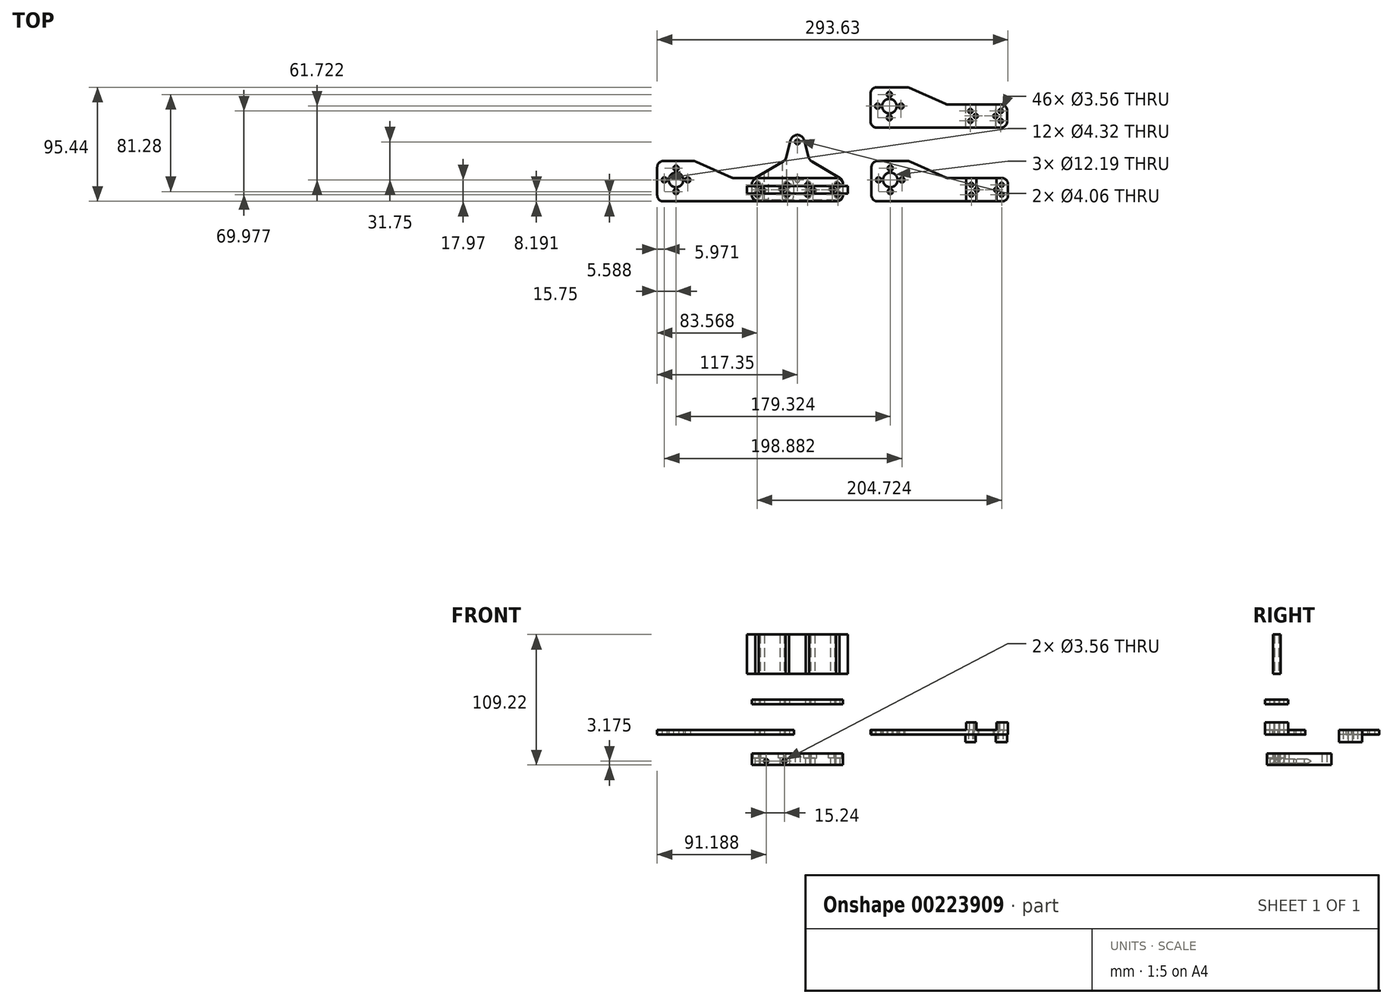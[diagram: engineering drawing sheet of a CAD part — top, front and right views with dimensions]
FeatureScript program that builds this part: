
annotation { "Feature Type Name" : "Feature", "Feature Type Description" : "" }
export const myFeature = defineFeature(function(context is Context, id is Id, definition is map)
    precondition{}
    {
        {
            var Q0;
            Q0=qCreatedBy(makeId("Top.planeOp"),FACE);
            var sketch = newSketch(context, id + "F0", { "sketchPlane" : qUnion([Q0])});
            skCircle(sketch, "E0", {"center": v(0, 37.5) * mm, "radius": 2.03 * mm});
            skCircle(sketch, "E1", {"center": v(0, 5.75) * mm, "radius": 2.03 * mm});
            skCircle(sketch, "E2", {"center": v(0, 37.5) * mm, "radius": 5.84 * mm});
            skLineSegment(sketch, "E3", {"start": v(-10.16, 22.26) * mm, "end": v(-5.64, 39.02) * mm});
            skLineSegment(sketch, "E4", {"start": v(10.16, 22.26) * mm, "end": v(5.64, 39.02) * mm});
            skPoint(sketch, "E5.orphan", {"position": v(0, 22.26) * mm});
            skLineSegment(sketch, "E6", {"start": v(-38.1, -10.76) * mm, "end": v(38.1, -10.76) * mm});
            skLineSegment(sketch, "E7", {"start": v(-38.1, -10.76) * mm, "end": v(-38.1, 5.75) * mm});
            skLineSegment(sketch, "E8", {"start": v(38.1, 5.75) * mm, "end": v(38.1, -10.76) * mm});
            skLineSegment(sketch, "E9", {"start": v(-10.16, 22.26) * mm, "end": v(10.16, 22.26) * mm});
            skLineSegment(sketch, "E10", {"start": v(-38.1, 5.75) * mm, "end": v(-10.16, 22.26) * mm});
            skLineSegment(sketch, "E11", {"start": v(10.16, 22.26) * mm, "end": v(38.1, 5.75) * mm});
            skPoint(sketch, "E12.centerSnap0", {"position": v(38.1, -2.5) * mm});
            skPoint(sketch, "E13.centerSnap0", {"position": v(-38.1, -2.5) * mm});
            skCircle(sketch, "E14.MirrorC", {"center": v(33.78, -6.63) * mm, "radius": 1.78 * mm});
            skCircle(sketch, "E15.MirrorC", {"center": v(33.78, 1.62) * mm, "radius": 1.78 * mm});
            skCircle(sketch, "E16", {"center": v(8.38, 1.62) * mm, "radius": 1.78 * mm});
            skCircle(sketch, "E17", {"center": v(8.38, -6.63) * mm, "radius": 1.78 * mm});
            skCircle(sketch, "E18.MirrorC", {"center": v(-8.38, -6.63) * mm, "radius": 1.78 * mm});
            skCircle(sketch, "E19.MirrorC", {"center": v(-33.78, -6.63) * mm, "radius": 1.78 * mm});
            skCircle(sketch, "E20.MirrorC", {"center": v(-33.78, 1.62) * mm, "radius": 1.78 * mm});
            skCircle(sketch, "E21.MirrorC", {"center": v(-8.38, 1.62) * mm, "radius": 1.78 * mm});
            skCircle(sketch, "E22", {"center": v(-29.3, -2.5) * mm, "radius": 1.78 * mm});
            skCircle(sketch, "E23", {"center": v(-12.87, -2.5) * mm, "radius": 1.78 * mm});
            skCircle(sketch, "E24.MirrorC", {"center": v(12.87, -2.5) * mm, "radius": 1.78 * mm});
            skCircle(sketch, "E25.MirrorC", {"center": v(29.3, -2.5) * mm, "radius": 1.78 * mm});
            skSolve(sketch);
        }
        {
            var Q0;
            Q0=qSketchRegion(id+"F0",true);
            extrude(context, id + "F1", {"entities" : qUnion([Q0]), "depth" : 9.65 * mm});
        }
        {
            var Q0;
            Q0=makeQuery(id+"FxuT3BSMLhrPvgB_1.opExtrude","SWEPT_EDGE",EDGE,{"disambiguationData":[OSD([sQuery(id+"FRq1eFHlobFPW3q_1.wireOp",EDGE,"58NqGU18-HprJ-QbKg-xDFZ-83wXZvhciFSB"),sQuery(id+"FRq1eFHlobFPW3q_1.wireOp",EDGE,"uo3OqS3Z-w3Q3-Ubee-oUpL-cwzrscQqbqLB")])]});
            var Q1;
            Q1=makeQuery(id+"FxuT3BSMLhrPvgB_1.opExtrude","SWEPT_EDGE",EDGE,{"disambiguationData":[OSD([sQuery(id+"FRq1eFHlobFPW3q_1.wireOp",EDGE,"0EPiVd3f-FInE-hob0-EaqF-tfDaMfGh4eWV.bottom"),sQuery(id+"FRq1eFHlobFPW3q_1.wireOp",EDGE,"uo3OqS3Z-w3Q3-Ubee-oUpL-cwzrscQqbqLB")])]});
            var Q2;
            Q2=makeQuery(id+"FxuT3BSMLhrPvgB_1.opExtrude","SWEPT_EDGE",EDGE,{"disambiguationData":[OSD([sQuery(id+"FRq1eFHlobFPW3q_1.wireOp",EDGE,"0EPiVd3f-FInE-hob0-EaqF-tfDaMfGh4eWV.bottom"),sQuery(id+"FRq1eFHlobFPW3q_1.wireOp",EDGE,"8aeSwGbv-ZD2Z-QxL9-UaCv-KycSeOo3iLFE")])]});
            var Q3;
            Q3=makeQuery(id+"FxuT3BSMLhrPvgB_1.opExtrude","SWEPT_EDGE",EDGE,{"disambiguationData":[OSD([sQuery(id+"FRq1eFHlobFPW3q_1.wireOp",EDGE,"8aeSwGbv-ZD2Z-QxL9-UaCv-KycSeOo3iLFE"),sQuery(id+"FRq1eFHlobFPW3q_1.wireOp",EDGE,"58NqGU18-HprJ-QbKg-xDFZ-83wXZvhciFSB")])]});
            var Q4;
            {var subQ0=sQuery(id+"F0.wireOp",EDGE,"E10");var subQ1=sQuery(id+"F0.wireOp",EDGE,"E7");Q4=makeQuery(id+"FLg3E5WfsGnaKrj_1.boolean.opBoolean","MERGE",EDGE,{"derivedFrom":[makeQuery(id+"F1.opExtrude","SWEPT_EDGE",EDGE,{"disambiguationData":[OSD([subQ1,subQ0])]}),makeQuery(id+"FLg3E5WfsGnaKrj_1.opExtrude","SWEPT_EDGE",EDGE,{"disambiguationData":[OSD([subQ1,subQ0])]})]});}
            var Q5;
            Q5=makeQuery(id+"F1.opExtrude","SWEPT_EDGE",EDGE,{"disambiguationData":[OSD([sQuery(id+"F0.wireOp",EDGE,"E3"),sQuery(id+"F0.wireOp",EDGE,"E9"),sQuery(id+"F0.wireOp",EDGE,"E10")])]});
            var Q6;
            Q6=makeQuery(id+"F1.opExtrude","SWEPT_EDGE",EDGE,{"disambiguationData":[OSD([sQuery(id+"F0.wireOp",EDGE,"E4"),sQuery(id+"F0.wireOp",EDGE,"E9"),sQuery(id+"F0.wireOp",EDGE,"E11")])]});
            var Q7;
            Q7=makeQuery(id+"F1.opExtrude","SWEPT_EDGE",EDGE,{"disambiguationData":[OSD([sQuery(id+"F0.wireOp",EDGE,"E6"),sQuery(id+"F0.wireOp",EDGE,"E7")])]});
            var Q8;
            Q8=makeQuery(id+"F1.opExtrude","SWEPT_EDGE",EDGE,{"disambiguationData":[OSD([sQuery(id+"F0.wireOp",EDGE,"E6"),sQuery(id+"F0.wireOp",EDGE,"E8")])]});
            var Q9;
            Q9=makeQuery(id+"F1.opExtrude","SWEPT_EDGE",EDGE,{"disambiguationData":[OSD([sQuery(id+"F0.wireOp",EDGE,"E8"),sQuery(id+"F0.wireOp",EDGE,"E11")])]});
            fillet(context, id + "F2", {"entities" : qUnion([Q0, Q1, Q2, Q3, Q4, Q5, Q6, Q7, Q8, Q9]), "radius" : 5.08 * mm, "tangentPropagation" : true, "allowEdgeOverflow" : false});
        }
        {
            var Q0;
            Q0=qCreatedBy(makeId("Top.planeOp"),FACE);
            cPlane(context, id + "F3", {"entities" : qUnion([Q0]), "cplaneType" : CPlaneType.OFFSET, "offset" : 25.4 * mm, "width" : 152.4 * mm, "height" : 152.4 * mm});
        }
        {
            var Q0;
            Q0=qCreatedBy(id+"F3.planeOp",FACE);
            var sketch = newSketch(context, id + "F4", { "sketchPlane" : qUnion([Q0])});
            skCircle(sketch, "E26.0", {"center": v(-33.78, 1.62) * mm, "radius": 1.78 * mm});
            skCircle(sketch, "E26.1", {"center": v(-8.38, 1.62) * mm, "radius": 1.78 * mm});
            skCircle(sketch, "E26.2", {"center": v(-8.38, -6.63) * mm, "radius": 1.78 * mm});
            skCircle(sketch, "E26.3", {"center": v(-33.78, -6.63) * mm, "radius": 1.78 * mm});
            skLineSegment(sketch, "E27", {"start": v(-3.05, -12.22) * mm, "end": v(-3.05, 7.21) * mm});
            skLineSegment(sketch, "E28", {"start": v(-85.85, 21.5) * mm, "end": v(-117.35, 21.5) * mm});
            skLineSegment(sketch, "E29", {"start": v(-117.35, 21.5) * mm, "end": v(-117.35, -12.22) * mm});
            skLineSegment(sketch, "E30", {"start": v(-117.35, -12.22) * mm, "end": v(-3.05, -12.22) * mm});
            skCircle(sketch, "E31.0", {"center": v(0, 5.75) * mm, "radius": 2.03 * mm, "construction": true});
            skCircle(sketch, "E32", {"center": v(-111.38, 5.75) * mm, "radius": 2.16 * mm});
            skCircle(sketch, "E33", {"center": v(-101.6, 5.75) * mm, "radius": 6.1 * mm});
            skCircle(sketch, "E34", {"center": v(-91.82, 5.75) * mm, "radius": 2.16 * mm});
            skCircle(sketch, "E35", {"center": v(-101.6, 15.53) * mm, "radius": 2.16 * mm});
            skCircle(sketch, "E36", {"center": v(-101.6, -4.03) * mm, "radius": 2.16 * mm});
            skLineSegment(sketch, "E37", {"start": v(-3.05, 7.21) * mm, "end": v(-53.85, 7.21) * mm});
            skLineSegment(sketch, "E38", {"start": v(-53.85, 7.21) * mm, "end": v(-85.85, 21.5) * mm});
            skCircle(sketch, "E39", {"center": v(-12.87, -2.5) * mm, "radius": 1.78 * mm});
            skPoint(sketch, "E39.centerSnap0", {"position": v(-3.05, -2.5) * mm});
            skCircle(sketch, "E40", {"center": v(-29.3, -2.5) * mm, "radius": 1.78 * mm});
            skSolve(sketch);
        }
        {
            var Q0;
            Q0=makeQuery(id+"F4.imprint","IMPRINT",FACE,{"disambiguationData":[TD([[makeQuery(id+"F4.imprint","IMPRINT",EDGE,{"derivedFrom":sQuery(id+"F4.wireOp",EDGE,"E26.0")}),-1.0]])]});
            extrude(context, id + "F5", {"entities" : qUnion([Q0]), "depth" : 3.8 * mm});
        }
        {
            var Q0;
            Q0=makeQuery(id+"F5.opExtrude","SWEPT_EDGE",EDGE,{"disambiguationData":[OSD([sQuery(id+"F4.wireOp",EDGE,"E28"),sQuery(id+"F4.wireOp",EDGE,"E29")])]});
            var Q1;
            Q1=makeQuery(id+"F5.opExtrude","SWEPT_EDGE",EDGE,{"disambiguationData":[OSD([sQuery(id+"F4.wireOp",EDGE,"E29"),sQuery(id+"F4.wireOp",EDGE,"E30")])]});
            var Q2;
            Q2=makeQuery(id+"F5.opExtrude","SWEPT_EDGE",EDGE,{"disambiguationData":[OSD([sQuery(id+"F4.wireOp",EDGE,"E28"),sQuery(id+"F4.wireOp",EDGE,"E38")])]});
            var Q3;
            Q3=makeQuery(id+"F5.opExtrude","SWEPT_EDGE",EDGE,{"disambiguationData":[OSD([sQuery(id+"F4.wireOp",EDGE,"E37"),sQuery(id+"F4.wireOp",EDGE,"E38")])]});
            var Q4;
            Q4=makeQuery(id+"F5.opExtrude","SWEPT_EDGE",EDGE,{"disambiguationData":[OSD([sQuery(id+"F4.wireOp",EDGE,"E27"),sQuery(id+"F4.wireOp",EDGE,"E37")])]});
            var Q5;
            Q5=makeQuery(id+"F5.opExtrude","SWEPT_EDGE",EDGE,{"disambiguationData":[OSD([sQuery(id+"F4.wireOp",EDGE,"E27"),sQuery(id+"F4.wireOp",EDGE,"E30")])]});
            fillet(context, id + "F6", {"entities" : qUnion([Q0, Q1, Q2, Q3, Q4, Q5]), "radius" : 5.08 * mm, "tangentPropagation" : true, "allowEdgeOverflow" : false});
        }
        {
            var Q0;
            Q0=qCreatedBy(id+"F3.planeOp",FACE);
            cPlane(context, id + "F7", {"entities" : qUnion([Q0]), "cplaneType" : CPlaneType.OFFSET, "offset" : 25.4 * mm, "width" : 152.4 * mm, "height" : 152.4 * mm});
        }
        {
            var Q0;
            Q0=qCreatedBy(id+"F7.planeOp",FACE);
            var sketch = newSketch(context, id + "F8", { "sketchPlane" : qUnion([Q0])});
            skLineSegment(sketch, "E41.0.2", {"start": v(-38.1, 2.85) * mm, "end": v(-38.1, -5.68) * mm});
            skLineSegment(sketch, "E41.0.6", {"start": v(38.1, -5.68) * mm, "end": v(38.1, 2.85) * mm});
            skLineSegment(sketch, "E42", {"start": v(38.1, 2.85) * mm, "end": v(38.1, 7.21) * mm});
            skLineSegment(sketch, "E43", {"start": v(38.1, 7.21) * mm, "end": v(-38.1, 7.21) * mm});
            skLineSegment(sketch, "E44", {"start": v(-38.1, 7.21) * mm, "end": v(-38.1, 2.85) * mm});
            skLineSegment(sketch, "E45", {"start": v(38.1, -5.68) * mm, "end": v(38.1, -12.22) * mm});
            skLineSegment(sketch, "E46", {"start": v(38.1, -12.22) * mm, "end": v(-38.1, -12.22) * mm});
            skLineSegment(sketch, "E47", {"start": v(-38.1, -12.22) * mm, "end": v(-38.1, -5.68) * mm});
            skCircle(sketch, "E48.0", {"center": v(-33.78, 1.62) * mm, "radius": 1.78 * mm});
            skCircle(sketch, "E48.1", {"center": v(-33.78, -6.63) * mm, "radius": 1.78 * mm});
            skCircle(sketch, "E48.2", {"center": v(-8.38, 1.62) * mm, "radius": 1.78 * mm});
            skCircle(sketch, "E48.3", {"center": v(-8.38, -6.63) * mm, "radius": 1.78 * mm});
            skCircle(sketch, "E48.4", {"center": v(8.38, 1.62) * mm, "radius": 1.78 * mm});
            skCircle(sketch, "E48.5", {"center": v(8.38, -6.63) * mm, "radius": 1.78 * mm});
            skCircle(sketch, "E48.6", {"center": v(33.78, 1.62) * mm, "radius": 1.78 * mm});
            skCircle(sketch, "E48.7", {"center": v(33.78, -6.63) * mm, "radius": 1.78 * mm});
            skCircle(sketch, "E49.0", {"center": v(-29.3, -2.5) * mm, "radius": 1.78 * mm});
            skCircle(sketch, "E49.1", {"center": v(-12.87, -2.5) * mm, "radius": 1.78 * mm});
            skCircle(sketch, "E50.MirrorC", {"center": v(12.87, -2.5) * mm, "radius": 1.78 * mm});
            skCircle(sketch, "E51.MirrorC", {"center": v(29.3, -2.5) * mm, "radius": 1.78 * mm});
            skSolve(sketch);
        }
        {
            var Q0;
            Q0 = qSketchRegion(id + "F8", true);
            extrude(context, id + "F9", {"entities" : qUnion([Q0]), "depth" : 3.8 * mm});
        }
        {
            var Q0;
            Q0=makeQuery(id+"F9.opExtrude","SWEPT_EDGE",EDGE,{"disambiguationData":[OSD([sQuery(id+"F8.wireOp",EDGE,"E42"),sQuery(id+"F8.wireOp",EDGE,"E43")])]});
            var Q1;
            Q1=makeQuery(id+"F9.opExtrude","SWEPT_EDGE",EDGE,{"disambiguationData":[OSD([sQuery(id+"F8.wireOp",EDGE,"E45"),sQuery(id+"F8.wireOp",EDGE,"E46")])]});
            var Q2;
            Q2=makeQuery(id+"F9.opExtrude","SWEPT_EDGE",EDGE,{"disambiguationData":[OSD([sQuery(id+"F8.wireOp",EDGE,"E43"),sQuery(id+"F8.wireOp",EDGE,"E44")])]});
            var Q3;
            Q3=makeQuery(id+"F9.opExtrude","SWEPT_EDGE",EDGE,{"disambiguationData":[OSD([sQuery(id+"F8.wireOp",EDGE,"E46"),sQuery(id+"F8.wireOp",EDGE,"E47")])]});
            fillet(context, id + "F10", {"entities" : qUnion([Q0, Q1, Q2, Q3]), "radius" : 5.08 * mm, "tangentPropagation" : true, "allowEdgeOverflow" : false});
        }
        {
            var Q0;
            Q0=qCreatedBy(makeId("Top.planeOp"),FACE);
            var sketch = newSketch(context, id + "F11", { "sketchPlane" : qUnion([Q0])});
            skLineSegment(sketch, "E52.bottom", {"start": v(-79.25, -25.05) * mm, "end": v(0, -25.05) * mm});
            skLineSegment(sketch, "E52.top", {"start": v(-79.25, -57.56) * mm, "end": v(0, -57.56) * mm});
            skLineSegment(sketch, "E52.left", {"start": v(-79.25, -25.05) * mm, "end": v(-79.25, -57.56) * mm});
            skLineSegment(sketch, "E52.right", {"start": v(0, -25.05) * mm, "end": v(0, -57.56) * mm});
            skSolve(sketch);
        }
        {
            var Q0;
            Q0=makeQuery(id+"F11.imprint","IMPRINT",FACE,{"disambiguationData":[TD([[makeQuery(id+"F11.imprint","IMPRINT",EDGE,{"derivedFrom":sQuery(id+"F11.wireOp",EDGE,"E52.bottom")}),-1.0]])]});
            extrude(context, id + "F12", {"entities" : qUnion([Q0]), "depth" : 6.35 * mm});
        }
        {
            var Q0;
            Q0=makeQuery(id+"F5.opExtrude","SWEPT_BODY",BODY,{"disambiguationData":[OSD([sQuery(id+"F4.wireOp",EDGE,"E26.0"),sQuery(id+"F4.wireOp",EDGE,"E26.1"),sQuery(id+"F4.wireOp",EDGE,"E26.2"),sQuery(id+"F4.wireOp",EDGE,"E26.3"),sQuery(id+"F4.wireOp",EDGE,"E27"),sQuery(id+"F4.wireOp",EDGE,"E28"),sQuery(id+"F4.wireOp",EDGE,"E29"),sQuery(id+"F4.wireOp",EDGE,"E30"),sQuery(id+"F4.wireOp",EDGE,"E32"),sQuery(id+"F4.wireOp",EDGE,"E33"),sQuery(id+"F4.wireOp",EDGE,"E34"),sQuery(id+"F4.wireOp",EDGE,"E35"),sQuery(id+"F4.wireOp",EDGE,"E36"),sQuery(id+"F4.wireOp",EDGE,"E37"),sQuery(id+"F4.wireOp",EDGE,"E38")])]});
            transform(context, id + "F13", {"entities" : qUnion([Q0]), "transformType" : TransformType.TRANSLATION_3D, "dx" : 179.32 * mm, "dy" : 0 * mm, "dz" : 0 * mm, "makeCopy" : true});
        }
        {
            var Q0;
            Q0=makeQuery(id+"F13.opPattern","COPY",FACE,{"derivedFrom":makeQuery(id+"F5.opExtrude","CAP_FACE",FACE,{"disambiguationData":[OSD([sQuery(id+"F4.wireOp",EDGE,"E26.0"),sQuery(id+"F4.wireOp",EDGE,"E26.1"),sQuery(id+"F4.wireOp",EDGE,"E26.2"),sQuery(id+"F4.wireOp",EDGE,"E26.3"),sQuery(id+"F4.wireOp",EDGE,"E27"),sQuery(id+"F4.wireOp",EDGE,"E28"),sQuery(id+"F4.wireOp",EDGE,"E29"),sQuery(id+"F4.wireOp",EDGE,"E30"),sQuery(id+"F4.wireOp",EDGE,"E32"),sQuery(id+"F4.wireOp",EDGE,"E33"),sQuery(id+"F4.wireOp",EDGE,"E34"),sQuery(id+"F4.wireOp",EDGE,"E35"),sQuery(id+"F4.wireOp",EDGE,"E36"),sQuery(id+"F4.wireOp",EDGE,"E37"),sQuery(id+"F4.wireOp",EDGE,"E38")])],"isStart":false}),"instanceName":"1"});
            var sketch = newSketch(context, id + "F14", { "sketchPlane" : qUnion([Q0])});
            skCircle(sketch, "E53.0", {"center": v(145.54, 1.62) * mm, "radius": 1.78 * mm});
            skCircle(sketch, "E54.0", {"center": v(145.54, -6.63) * mm, "radius": 1.78 * mm});
            skCircle(sketch, "E55.0", {"center": v(170.94, 1.62) * mm, "radius": 1.78 * mm});
            skCircle(sketch, "E56.0", {"center": v(170.94, -6.63) * mm, "radius": 1.78 * mm});
            skLineSegment(sketch, "E57.bottom", {"start": v(149.86, 7.21) * mm, "end": v(141.22, 7.21) * mm});
            skLineSegment(sketch, "E57.top", {"start": v(149.86, -12.22) * mm, "end": v(141.22, -12.22) * mm});
            skLineSegment(sketch, "E57.left", {"start": v(149.86, 7.21) * mm, "end": v(149.86, -12.22) * mm});
            skLineSegment(sketch, "E57.right", {"start": v(141.22, 7.21) * mm, "end": v(141.22, -12.22) * mm});
            skPoint(sketch, "E57.middle", {"position": v(145.54, -2.5) * mm});
            skLineSegment(sketch, "E58.left", {"start": v(166.62, 7.21) * mm, "end": v(166.62, -12.22) * mm});
            skLineSegment(sketch, "E59.0", {"start": v(171.2, 7.21) * mm, "end": v(166.62, 7.21) * mm});
            skArc(sketch, "E59.1", {"start": v(176.28, 2.13) * mm, "mid": v(174.79, 5.72) * mm, "end": v(171.2, 7.21) * mm});
            skLineSegment(sketch, "E59.2", {"start": v(176.28, -7.14) * mm, "end": v(176.28, 2.13) * mm});
            skArc(sketch, "E59.3", {"start": v(171.2, -12.22) * mm, "mid": v(174.79, -10.73) * mm, "end": v(176.28, -7.14) * mm});
            skLineSegment(sketch, "E59.4", {"start": v(141.22, -12.22) * mm, "end": v(149.86, -12.22) * mm});
            skLineSegment(sketch, "E60.trimOffspring", {"start": v(166.62, -12.22) * mm, "end": v(171.2, -12.22) * mm});
            skPoint(sketch, "E61.orphan", {"position": v(126.56, 7.21) * mm});
            skPoint(sketch, "E62.orphan", {"position": v(67.06, -12.22) * mm});
            skSolve(sketch);
        }
        {
            var Q0;
            Q0 = qSketchRegion(id + "F14", true);
            extrude(context, id + "F15", {"entities" : qUnion([Q0]), "operationType" : NewBodyOperationType.ADD, "depth" : 6.35 * mm});
        }
        {
            var Q0;
            Q0=makeQuery(id+"F5.opExtrude","SWEPT_BODY",BODY,{"disambiguationData":[OSD([sQuery(id+"F4.wireOp",EDGE,"E26.0"),sQuery(id+"F4.wireOp",EDGE,"E26.1"),sQuery(id+"F4.wireOp",EDGE,"E26.2"),sQuery(id+"F4.wireOp",EDGE,"E26.3"),sQuery(id+"F4.wireOp",EDGE,"E27"),sQuery(id+"F4.wireOp",EDGE,"E28"),sQuery(id+"F4.wireOp",EDGE,"E29"),sQuery(id+"F4.wireOp",EDGE,"E30"),sQuery(id+"F4.wireOp",EDGE,"E32"),sQuery(id+"F4.wireOp",EDGE,"E33"),sQuery(id+"F4.wireOp",EDGE,"E34"),sQuery(id+"F4.wireOp",EDGE,"E35"),sQuery(id+"F4.wireOp",EDGE,"E36"),sQuery(id+"F4.wireOp",EDGE,"E37"),sQuery(id+"F4.wireOp",EDGE,"E38")])]});
            transform(context, id + "F16", {"entities" : qUnion([Q0]), "transformType" : TransformType.TRANSLATION_3D, "dx" : 178.56 * mm, "dy" : 61.72 * mm, "dz" : 0 * mm, "makeCopy" : true});
        }
        {
            var Q0;
            Q0=makeQuery(id+"F16.opPattern","COPY",FACE,{"derivedFrom":makeQuery(id+"F5.opExtrude","CAP_FACE",FACE,{"disambiguationData":[OSD([sQuery(id+"F4.wireOp",EDGE,"E26.0"),sQuery(id+"F4.wireOp",EDGE,"E26.1"),sQuery(id+"F4.wireOp",EDGE,"E26.2"),sQuery(id+"F4.wireOp",EDGE,"E26.3"),sQuery(id+"F4.wireOp",EDGE,"E27"),sQuery(id+"F4.wireOp",EDGE,"E28"),sQuery(id+"F4.wireOp",EDGE,"E29"),sQuery(id+"F4.wireOp",EDGE,"E30"),sQuery(id+"F4.wireOp",EDGE,"E32"),sQuery(id+"F4.wireOp",EDGE,"E33"),sQuery(id+"F4.wireOp",EDGE,"E34"),sQuery(id+"F4.wireOp",EDGE,"E35"),sQuery(id+"F4.wireOp",EDGE,"E36"),sQuery(id+"F4.wireOp",EDGE,"E37"),sQuery(id+"F4.wireOp",EDGE,"E38")])],"isStart":true}),"instanceName":"1"});
            var sketch = newSketch(context, id + "F17", { "sketchPlane" : qUnion([Q0])});
            skLineSegment(sketch, "E63.0", {"start": v(170.43, -68.93) * mm, "end": v(165.86, -68.93) * mm});
            skArc(sketch, "E63.1", {"start": v(170.43, -68.93) * mm, "mid": v(174.03, -67.44) * mm, "end": v(175.51, -63.85) * mm});
            skLineSegment(sketch, "E63.2", {"start": v(175.51, -54.58) * mm, "end": v(175.51, -63.85) * mm});
            skArc(sketch, "E63.3", {"start": v(175.51, -54.58) * mm, "mid": v(174.03, -50.99) * mm, "end": v(170.43, -49.5) * mm});
            skLineSegment(sketch, "E63.4", {"start": v(140.46, -49.5) * mm, "end": v(149.1, -49.5) * mm});
            skLineSegment(sketch, "E64", {"start": v(165.86, -68.93) * mm, "end": v(165.86, -49.5) * mm});
            skLineSegment(sketch, "E65", {"start": v(140.46, -68.93) * mm, "end": v(140.46, -49.5) * mm});
            skLineSegment(sketch, "E66", {"start": v(149.1, -68.93) * mm, "end": v(149.1, -49.5) * mm});
            skCircle(sketch, "E67.0", {"center": v(170.18, -63.34) * mm, "radius": 1.78 * mm});
            skCircle(sketch, "E67.1", {"center": v(170.18, -55.09) * mm, "radius": 1.78 * mm});
            skCircle(sketch, "E67.2", {"center": v(144.78, -55.09) * mm, "radius": 1.78 * mm});
            skCircle(sketch, "E67.3", {"center": v(144.78, -63.34) * mm, "radius": 1.78 * mm});
            skLineSegment(sketch, "E68.trimOffspring", {"start": v(165.86, -49.5) * mm, "end": v(170.43, -49.5) * mm});
            skLineSegment(sketch, "E69.trimOffspring", {"start": v(149.1, -68.93) * mm, "end": v(140.46, -68.93) * mm});
            skPoint(sketch, "E70.orphan", {"position": v(125.8, -68.93) * mm});
            skPoint(sketch, "E71.orphan", {"position": v(66.3, -49.5) * mm});
            skSolve(sketch);
        }
        {
            var Q0;
            Q0 = qSketchRegion(id + "F17", true);
            extrude(context, id + "F18", {"entities" : qUnion([Q0]), "operationType" : NewBodyOperationType.ADD, "depth" : 6.35 * mm});
        }
        {
            var Q0;
            Q0=makeQuery(id+"F1.opExtrude","CAP_FACE",FACE,{"disambiguationData":[OSD([sQuery(id+"F0.wireOp",EDGE,"E0"),sQuery(id+"F0.wireOp",EDGE,"E1"),sQuery(id+"F0.wireOp",EDGE,"E2"),sQuery(id+"F0.wireOp",EDGE,"E3"),sQuery(id+"F0.wireOp",EDGE,"E4"),sQuery(id+"F0.wireOp",EDGE,"E6"),sQuery(id+"F0.wireOp",EDGE,"E7"),sQuery(id+"F0.wireOp",EDGE,"E8"),sQuery(id+"F0.wireOp",EDGE,"E10"),sQuery(id+"F0.wireOp",EDGE,"E11"),sQuery(id+"F0.wireOp",EDGE,"E14.MirrorC"),sQuery(id+"F0.wireOp",EDGE,"E15.MirrorC"),sQuery(id+"F0.wireOp",EDGE,"E16"),sQuery(id+"F0.wireOp",EDGE,"E17"),sQuery(id+"F0.wireOp",EDGE,"E18.MirrorC"),sQuery(id+"F0.wireOp",EDGE,"E19.MirrorC"),sQuery(id+"F0.wireOp",EDGE,"E20.MirrorC"),sQuery(id+"F0.wireOp",EDGE,"E21.MirrorC")])],"isStart":false});
            var sketch = newSketch(context, id + "F19", { "sketchPlane" : qUnion([Q0])});
            skArc(sketch, "E72", {"start": v(-10.02, -1.1) * mm, "mid": v(-6.05, 3.77) * mm, "end": v(-11.23, 0.21) * mm});
            skArc(sketch, "E73", {"start": v(-30.94, 0.21) * mm, "mid": v(-36.12, 3.77) * mm, "end": v(-32.14, -1.1) * mm});
            skArc(sketch, "E74", {"start": v(-11.23, -5.22) * mm, "mid": v(-6.05, -8.78) * mm, "end": v(-10.02, -3.91) * mm});
            skArc(sketch, "E75.MirrorC", {"start": v(30.94, 0.21) * mm, "mid": v(36.12, 3.77) * mm, "end": v(32.14, -1.1) * mm});
            skArc(sketch, "E76.MirrorC", {"start": v(32.14, -3.91) * mm, "mid": v(36.12, -8.78) * mm, "end": v(30.94, -5.22) * mm});
            skArc(sketch, "E77.MirrorC", {"start": v(10.02, -1.1) * mm, "mid": v(6.05, 3.77) * mm, "end": v(11.23, 0.21) * mm});
            skArc(sketch, "E78.MirrorC", {"start": v(11.23, -5.22) * mm, "mid": v(6.05, -8.78) * mm, "end": v(10.02, -3.91) * mm});
            skCircle(sketch, "E79.0", {"center": v(-29.3, -2.5) * mm, "radius": 1.78 * mm});
            skCircle(sketch, "E79.1", {"center": v(-12.87, -2.5) * mm, "radius": 1.78 * mm});
            skCircle(sketch, "E79.2", {"center": v(12.87, -2.5) * mm, "radius": 1.78 * mm});
            skCircle(sketch, "E79.3", {"center": v(29.3, -2.5) * mm, "radius": 1.78 * mm});
            skArc(sketch, "E80", {"start": v(-32.14, -1.1) * mm, "mid": v(-32.47, -2.5) * mm, "end": v(-32.14, -3.91) * mm});
            skArc(sketch, "E81", {"start": v(-10.02, -3.91) * mm, "mid": v(-9.7, -2.5) * mm, "end": v(-10.02, -1.1) * mm});
            skArc(sketch, "E82", {"start": v(10.02, -1.1) * mm, "mid": v(9.7, -2.5) * mm, "end": v(10.02, -3.91) * mm});
            skArc(sketch, "E83", {"start": v(30.94, 0.21) * mm, "mid": v(26.12, -2.5) * mm, "end": v(30.94, -5.22) * mm});
            skArc(sketch, "E84.trimOffspring", {"start": v(-30.94, -5.22) * mm, "mid": v(-26.12, -2.5) * mm, "end": v(-30.94, 0.21) * mm});
            skPoint(sketch, "E85.center.orphan", {"position": v(-33.78, -6.63) * mm});
            skArc(sketch, "E86.trimOffspring", {"start": v(-11.23, 0.21) * mm, "mid": v(-16.04, -2.5) * mm, "end": v(-11.23, -5.22) * mm});
            skArc(sketch, "E87.trimOffspring", {"start": v(11.23, -5.22) * mm, "mid": v(16.04, -2.5) * mm, "end": v(11.23, 0.21) * mm});
            skArc(sketch, "E88.trimOffspring", {"start": v(32.14, -3.91) * mm, "mid": v(32.47, -2.5) * mm, "end": v(32.14, -1.1) * mm});
            skArc(sketch, "E89", {"start": v(-32.14, -3.91) * mm, "mid": v(-36.12, -8.78) * mm, "end": v(-30.94, -5.22) * mm});
            skSolve(sketch);
        }
        {
            var Q0;
            Q0 = qSketchRegion(id + "F19", true);
            extrude(context, id + "F20", {"entities" : qUnion([Q0]), "operationType" : NewBodyOperationType.REMOVE, "oppositeDirection" : true, "depth" : 3.8 * mm});
        }
        {
            var Q0;
            Q0=makeQuery(id+"F12.opExtrude","SWEPT_FACE",FACE,{"disambiguationData":[OSD([sQuery(id+"F11.wireOp",EDGE,"E52.top")])]});
            var sketch = newSketch(context, id + "F21", { "sketchPlane" : qUnion([Q0])});
            skCircle(sketch, "E90", {"center": v(-68.33, 3.18) * mm, "radius": 1.78 * mm});
            skPoint(sketch, "E90.centerSnap0", {"position": v(-79.25, 3.18) * mm});
            skCircle(sketch, "E91", {"center": v(-53.09, 3.18) * mm, "radius": 1.78 * mm});
            skCircle(sketch, "E92", {"center": v(-10.92, 3.18) * mm, "radius": 1.78 * mm});
            skCircle(sketch, "E93", {"center": v(-26.16, 3.18) * mm, "radius": 1.78 * mm});
            skSolve(sketch);
        }
        {
            var Q0;
            Q0 = qSketchRegion(id + "F21", true);
            extrude(context, id + "F22", {"entities" : qUnion([Q0]), "operationType" : NewBodyOperationType.REMOVE, "endBound" : BoundingType.THROUGH_ALL, "oppositeDirection" : true, "depth" : 25.4 * mm});
        }
        {
            var Q0;
            Q0=makeQuery(id+"F12.opExtrude","SWEPT_BODY",BODY,{"disambiguationData":[OSD([sQuery(id+"F11.wireOp",EDGE,"E52.bottom"),sQuery(id+"F11.wireOp",EDGE,"E52.top"),sQuery(id+"F11.wireOp",EDGE,"E52.left"),sQuery(id+"F11.wireOp",EDGE,"E52.right")])]});
            deleteBodies(context, id + "F23", {"entities" : qUnion([Q0])});
        }
        {
            var Q0;
            Q0=qCreatedBy(id+"F7.planeOp",FACE);
            cPlane(context, id + "F24", {"entities" : qUnion([Q0]), "cplaneType" : CPlaneType.OFFSET, "offset" : 25.4 * mm, "width" : 152.4 * mm, "height" : 152.4 * mm});
        }
        {
            var Q0;
            Q0=qCreatedBy(id+"F24.planeOp",FACE);
            var sketch = newSketch(context, id + "F25", { "sketchPlane" : qUnion([Q0])});
            skLineSegment(sketch, "E94.bottom", {"start": v(42.28, -5.68) * mm, "end": v(35.28, -5.68) * mm});
            skLineSegment(sketch, "E94.top", {"start": v(42.28, 0.67) * mm, "end": v(35.28, 0.67) * mm});
            skLineSegment(sketch, "E94.left", {"start": v(42.28, -5.68) * mm, "end": v(42.28, 0.67) * mm});
            skLineSegment(sketch, "E94.right", {"start": v(-42.28, -5.68) * mm, "end": v(-42.28, 0.67) * mm});
            skPoint(sketch, "E94.middle", {"position": v(0, -2.5) * mm});
            skCircle(sketch, "E95.0", {"center": v(-29.3, -2.5) * mm, "radius": 1.78 * mm});
            skCircle(sketch, "E95.1", {"center": v(-12.87, -2.5) * mm, "radius": 1.78 * mm});
            skCircle(sketch, "E95.2", {"center": v(12.87, -2.5) * mm, "radius": 1.78 * mm});
            skCircle(sketch, "E95.3", {"center": v(29.3, -2.5) * mm, "radius": 1.78 * mm});
            skArc(sketch, "E96.0", {"start": v(-35.28, 0.67) * mm, "mid": v(-33.78, -0.16) * mm, "end": v(-32.28, 0.67) * mm});
            skArc(sketch, "E96.1", {"start": v(-32.28, -5.68) * mm, "mid": v(-33.78, -4.85) * mm, "end": v(-35.28, -5.68) * mm});
            skArc(sketch, "E96.2", {"start": v(-6.88, -5.68) * mm, "mid": v(-8.38, -4.85) * mm, "end": v(-9.88, -5.68) * mm});
            skArc(sketch, "E96.3", {"start": v(-9.88, 0.67) * mm, "mid": v(-8.38, -0.16) * mm, "end": v(-6.88, 0.67) * mm});
            skArc(sketch, "E96.4", {"start": v(6.88, 0.67) * mm, "mid": v(8.38, -0.16) * mm, "end": v(9.88, 0.67) * mm});
            skArc(sketch, "E96.5", {"start": v(9.88, -5.68) * mm, "mid": v(8.38, -4.85) * mm, "end": v(6.88, -5.68) * mm});
            skArc(sketch, "E96.6", {"start": v(35.28, -5.68) * mm, "mid": v(33.78, -4.85) * mm, "end": v(32.28, -5.68) * mm});
            skArc(sketch, "E96.7", {"start": v(32.28, 0.67) * mm, "mid": v(33.78, -0.16) * mm, "end": v(35.28, 0.67) * mm});
            skLineSegment(sketch, "E97.trimOffspring", {"start": v(-35.28, 0.67) * mm, "end": v(-42.28, 0.67) * mm});
            skLineSegment(sketch, "E98.trimOffspring", {"start": v(-9.88, 0.67) * mm, "end": v(-32.28, 0.67) * mm});
            skLineSegment(sketch, "E99.trimOffspring", {"start": v(6.88, 0.67) * mm, "end": v(-6.88, 0.67) * mm});
            skLineSegment(sketch, "E100.trimOffspring", {"start": v(32.28, 0.67) * mm, "end": v(9.88, 0.67) * mm});
            skLineSegment(sketch, "E101.trimOffspring", {"start": v(-35.28, -5.68) * mm, "end": v(-42.28, -5.68) * mm});
            skLineSegment(sketch, "E102.trimOffspring", {"start": v(-9.88, -5.68) * mm, "end": v(-32.28, -5.68) * mm});
            skLineSegment(sketch, "E103.trimOffspring", {"start": v(6.88, -5.68) * mm, "end": v(-6.88, -5.68) * mm});
            skLineSegment(sketch, "E104.trimOffspring", {"start": v(32.28, -5.68) * mm, "end": v(9.88, -5.68) * mm});
            skSolve(sketch);
        }
        {
            var Q0;
            Q0 = qSketchRegion(id + "F25", true);
            extrude(context, id + "F26", {"entities" : qUnion([Q0]), "depth" : 33.02 * mm});
        }
        {
            var Q0;
            Q0=makeQuery(id+"F16.opPattern","COPY",FACE,{"derivedFrom":makeQuery(id+"F5.opExtrude","CAP_FACE",FACE,{"disambiguationData":[OSD([sQuery(id+"F4.wireOp",EDGE,"E26.0"),sQuery(id+"F4.wireOp",EDGE,"E26.1"),sQuery(id+"F4.wireOp",EDGE,"E26.2"),sQuery(id+"F4.wireOp",EDGE,"E26.3"),sQuery(id+"F4.wireOp",EDGE,"E27"),sQuery(id+"F4.wireOp",EDGE,"E28"),sQuery(id+"F4.wireOp",EDGE,"E29"),sQuery(id+"F4.wireOp",EDGE,"E30"),sQuery(id+"F4.wireOp",EDGE,"E32"),sQuery(id+"F4.wireOp",EDGE,"E33"),sQuery(id+"F4.wireOp",EDGE,"E34"),sQuery(id+"F4.wireOp",EDGE,"E35"),sQuery(id+"F4.wireOp",EDGE,"E36"),sQuery(id+"F4.wireOp",EDGE,"E37"),sQuery(id+"F4.wireOp",EDGE,"E38"),sQuery(id+"F4.wireOp",EDGE,"E39"),sQuery(id+"F4.wireOp",EDGE,"E40")])],"isStart":false}),"instanceName":"1"});
            var sketch = newSketch(context, id + "F27", { "sketchPlane" : qUnion([Q0])});
            skCircle(sketch, "E105.0", {"center": v(149.27, 59.22) * mm, "radius": 1.78 * mm});
            skCircle(sketch, "E106.0", {"center": v(165.7, 59.22) * mm, "radius": 1.78 * mm});
            skSolve(sketch);
        }
        {
            var Q0;
            Q0 = qSketchRegion(id + "F27", true);
            extrude(context, id + "F28", {"entities" : qUnion([Q0]), "operationType" : NewBodyOperationType.REMOVE, "endBound" : BoundingType.THROUGH_ALL, "oppositeDirection" : true, "depth" : 25.4 * mm});
        }
        {
            var Q0;
            Q0=makeQuery(id+"F13.opPattern","COPY",FACE,{"derivedFrom":makeQuery(id+"F5.opExtrude","CAP_FACE",FACE,{"disambiguationData":[OSD([sQuery(id+"F4.wireOp",EDGE,"E26.0"),sQuery(id+"F4.wireOp",EDGE,"E26.1"),sQuery(id+"F4.wireOp",EDGE,"E26.2"),sQuery(id+"F4.wireOp",EDGE,"E26.3"),sQuery(id+"F4.wireOp",EDGE,"E27"),sQuery(id+"F4.wireOp",EDGE,"E28"),sQuery(id+"F4.wireOp",EDGE,"E29"),sQuery(id+"F4.wireOp",EDGE,"E30"),sQuery(id+"F4.wireOp",EDGE,"E32"),sQuery(id+"F4.wireOp",EDGE,"E33"),sQuery(id+"F4.wireOp",EDGE,"E34"),sQuery(id+"F4.wireOp",EDGE,"E35"),sQuery(id+"F4.wireOp",EDGE,"E36"),sQuery(id+"F4.wireOp",EDGE,"E37"),sQuery(id+"F4.wireOp",EDGE,"E38"),sQuery(id+"F4.wireOp",EDGE,"E39"),sQuery(id+"F4.wireOp",EDGE,"E40")])],"isStart":true}),"instanceName":"1"});
            var sketch = newSketch(context, id + "F29", { "sketchPlane" : qUnion([Q0])});
            skCircle(sketch, "E107.0", {"center": v(166.46, 2.5) * mm, "radius": 1.78 * mm});
            skCircle(sketch, "E107.1", {"center": v(150.03, 2.5) * mm, "radius": 1.78 * mm});
            skSolve(sketch);
        }
        {
            var Q0;
            Q0 = qSketchRegion(id + "F29", true);
            extrude(context, id + "F30", {"entities" : qUnion([Q0]), "operationType" : NewBodyOperationType.REMOVE, "endBound" : BoundingType.THROUGH_ALL, "oppositeDirection" : true, "depth" : 25.4 * mm});
        }
    });
